# Revit family: Hager-UNIVERS-Hollow_wall-IP30-With_Cover-Without_DIN-NoHosted-AT-de
name_source: partatom
category: Electrical Equipment
units: mm (PartAtom-declared; Revit-internal decimal feet)

## family parameters
Always vertical = Yes
Cut with Voids When Loaded = No
Maintain Annotation Orientation = No
Panel Configuration = Two Columns, Circuits Across
Part Type = Panelboard
Room Calculation Point = No
Round Connector Dimension = Use Diameter
Shared = No
Work Plane-Based = Yes

## types (1)
- UNIVERS-Hollow_wall_W853_H853_D125_12_Modular_Spacing-FWU53S
    BC_METADATA = {"ObjectGuid":"bc35c96e-cb38-443e-833d-0616858cb9ac","ModelGuid":"8af03f69-2293-4735-a617-cc53adf55621","VariantGuid":"8b6e323b-1b53-409a-a940-11b5a7fc5337","Revision":"#4","VariantName":"Template-Enclosure_EU-EC000214"}
    BC_MODEL_ID = 1554440
    BC_OBJECT_ID = 513922
    BC_OBJECT_VERSION = #3
    BC_VARIANT_ID = 1179174
    Code hager = ADD-EC000214_EU
    Default Elevation = 1200 mm
    EF000003 - Montageart = Hohlwand
    EF000007 - Farbe = weiß
    EF000008 - Breite = 853 mm  [stored 2.79856 ft]
    EF000024 - UV-beständig = No
    EF000040 - Höhe = 853 mm  [stored 2.79856 ft]
    EF000049 - Tiefe = 125 mm  [stored 0.410105 ft]
    EF000116 - RAL-Nummer = 9010
    EF000118 - Mit Montageplatte = No
    EF000218 - Einbautiefe = 112 mm  [stored 0.367454 ft]
    EF000266 - Anzahl der Reihen = 5
    EF000332 - Einbauhöhe = 802 mm  [stored 2.63123 ft]
    EF000846 - Einbaubreite = 810 mm
    EF001062 - EMV-Ausführung = No
    EF001088 - Anbaumöglichkeit = Yes
    EF001131 - Innentiefe = 0 mm  [stored 0 ft]
    EF001134 - DIN-Schiene = No
    EF002950 - Breite in Teilungseinheiten = 12
    EF004462 - Art der Schließung = sonstige
    EF005474 - Schutzart (IP) = IP30
    EF006244 - Transparenter Deckel/Tür = No
    EF006306 - Mit Schloss = No
    EF009212 - Ausführung Deckel = mit Ausschnitt
    EF015776 - Erdungsklemmenblock = Yes
    EF015777 - Neutralleiterklemmenblock = No
    EF015941 - Signaldurchlassende Tür = No
    ETIM class code = EC000214
    ETIM class name = Small distribution board
    HG000001-Anzahl der Spalten = 3
    HG000002-Mit tür = Yes
    HG000003-Bereich = UNIVERS
    HG000004-Herstellerreferenz = FWU53S
    HG000005-Dicke = 2 mm  [stored 0.00656168 ft]
    HG000006-Unterputz = Yes
    HG000007-Anzahl der leeren Spalten = 0
    HG000008-Anzahl der leeren Reihen = 0
    HG000009-Doppelflügeligen Tür = Yes
    HG000010-Asymmetrische Türen = Yes
    HG000011-Leere Reihen von unten = No
    HG000012-Türschwenkwinkel = 90.00°
    HG000013-Tür links = No
    HG000014-Tür rechts = Yes
    HG000015-Sichtbarkeit der Türöffnung = Yes
    HG000016-3D-Türsichtbarkeit = Yes
    HG000017-Distanz zwischen den Polen = 18 mm  [stored 0.0590551 ft]
    HG000060-RAL-number = 9010
    HG000099-Onfly Template ID-de-AT = 507532
    HGEF000266-Anzahl der Reihen = 5
    HGEF0002950-Breite in Teilungseinheiten = 12
    Manufacturer = Hager
    Name = UNIVERS-Hollow_wall-IP30-With_Cover-Without_DIN-AT
    Name BIM&CO = Electricity
    Name hager = ADD_Enclosures_EC000214
    Reference = UNIVERS-Hollow_wall_W853_H853_D125_12_Modular_Spacing-FWU53S
    Uniformat = Low Tension Service & Dist.
    Uniformat code = D501001

note: [stored X ft] marks values corroborated as IEEE doubles in the binary element streams (Revit-internal decimal feet)

## geometry (parser evidence)
native form markers: Sweep x17
no freeform markers — native parametric forms only
